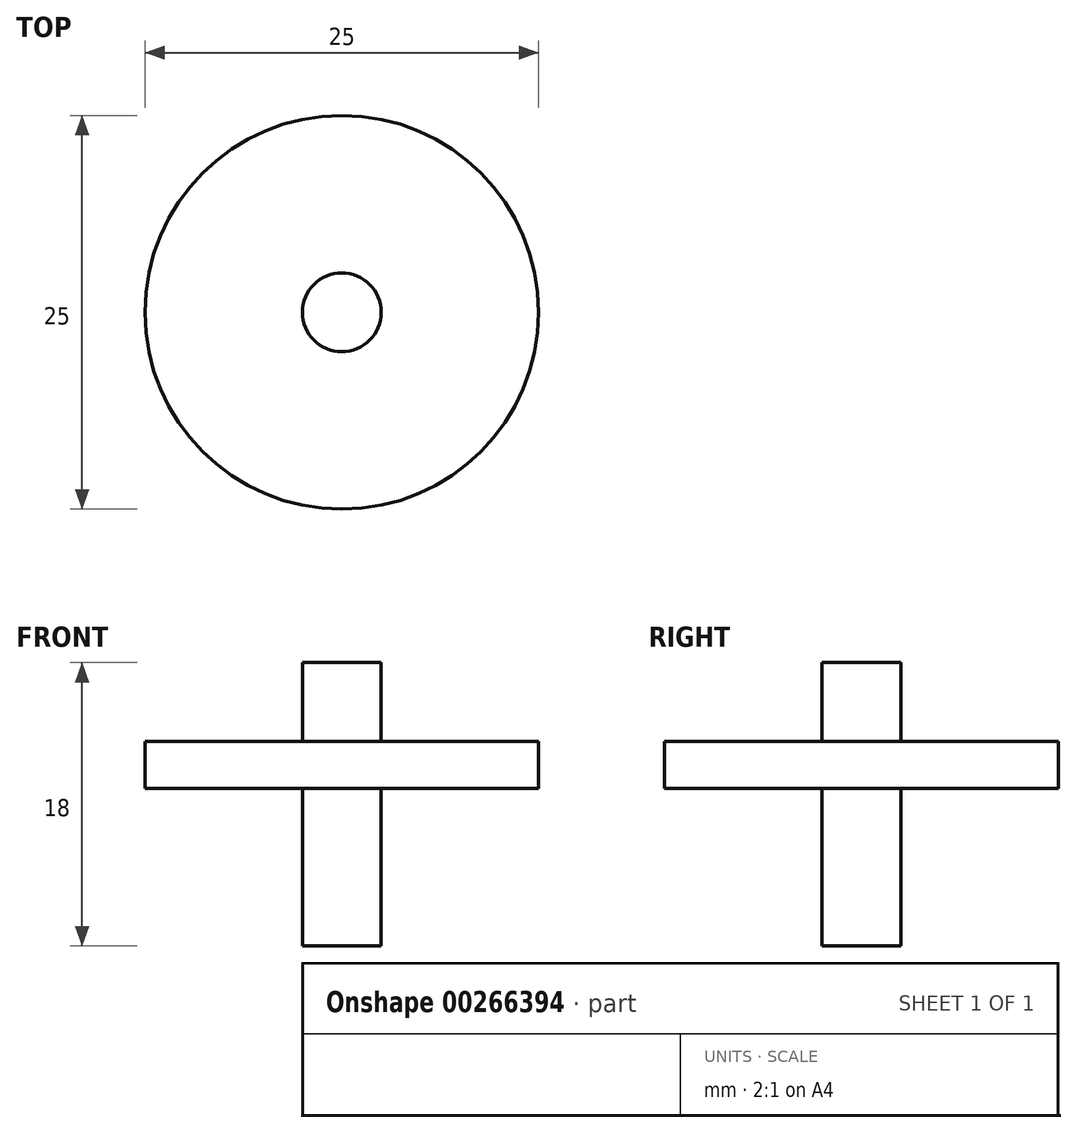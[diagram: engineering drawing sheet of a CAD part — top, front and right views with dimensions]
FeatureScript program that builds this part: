
annotation { "Feature Type Name" : "Feature", "Feature Type Description" : "" }
export const myFeature = defineFeature(function(context is Context, id is Id, definition is map)
    precondition{}
    {
        {
            var Q0;
            Q0=qCreatedBy(makeId("Top.planeOp"),FACE);
            var sketch = newSketch(context, id + "F0", { "sketchPlane" : qUnion([Q0])});
            skCircle(sketch, "E0", {"center": v(0, 0) * mm, "radius": 12.5 * mm});
            skCircle(sketch, "E1", {"center": v(0, 0) * mm, "radius": 2.5 * mm});
            skSolve(sketch);
        }
        {
            var Q0;
            Q0=makeQuery(id+"F0.imprint","IMPRINT",FACE,{"disambiguationData":[TD([[makeQuery(id+"F0.imprint","IMPRINT",EDGE,{"derivedFrom":sQuery(id+"F0.wireOp",EDGE,"E0")}),1.0]])]});
            extrude(context, id + "F1", {"entities" : qUnion([Q0]), "depth" : 1.5 * mm, "offsetDistance" : 25 * mm, "hasSecondDirection" : true, "secondDirectionOppositeDirection" : true, "secondDirectionDepth" : 1.5 * mm});
        }
        {
            var Q0;
            Q0=makeQuery(id+"F0.imprint","IMPRINT",FACE,{"disambiguationData":[TD([[makeQuery(id+"F0.imprint","IMPRINT",EDGE,{"derivedFrom":sQuery(id+"F0.wireOp",EDGE,"E1")}),1.0]])]});
            extrude(context, id + "F2", {"entities" : qUnion([Q0]), "operationType" : NewBodyOperationType.ADD, "depth" : 6.5 * mm, "offsetDistance" : 25 * mm, "hasSecondDirection" : true, "secondDirectionOppositeDirection" : true, "secondDirectionDepth" : 11.5 * mm});
        }
    });
